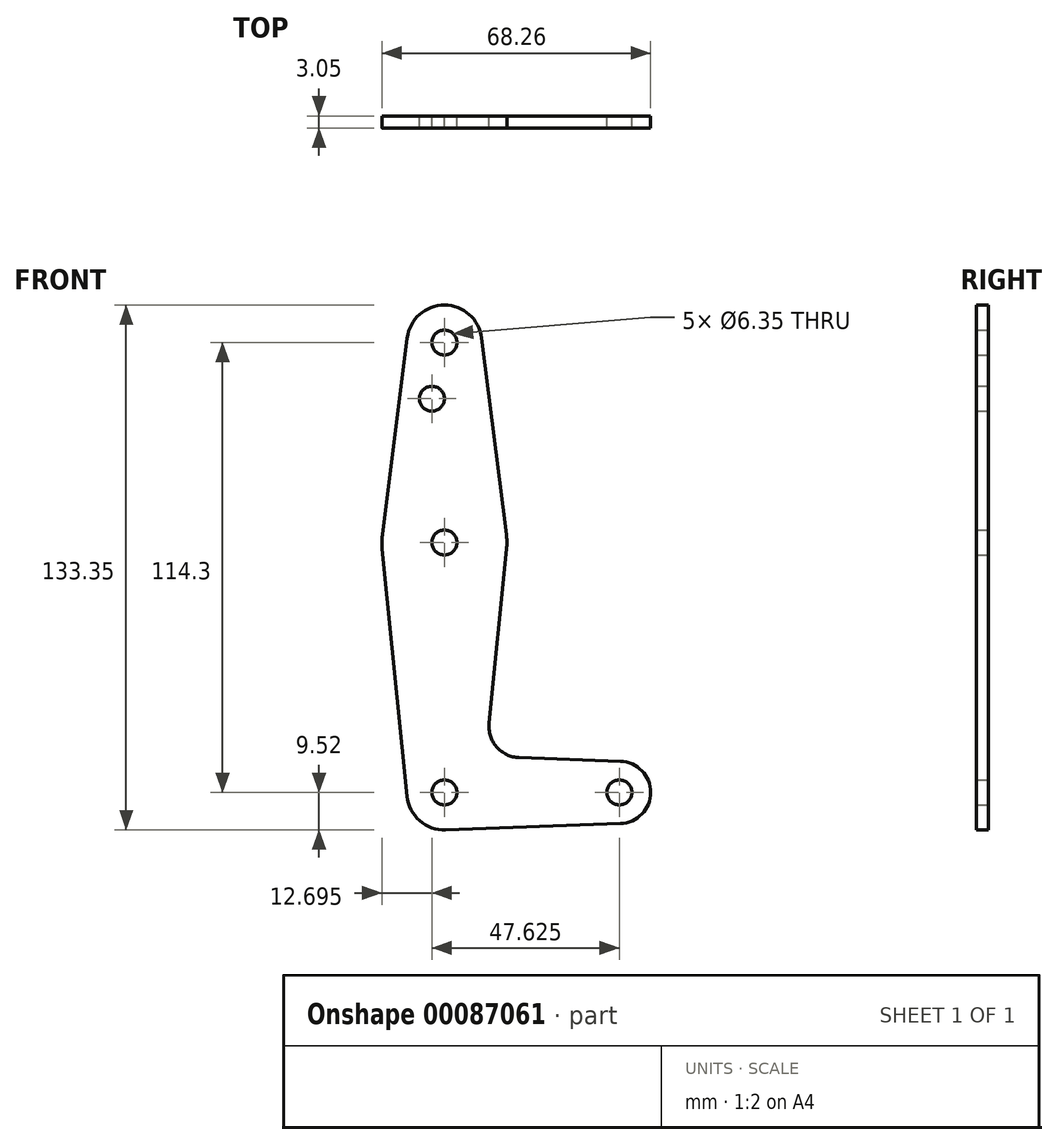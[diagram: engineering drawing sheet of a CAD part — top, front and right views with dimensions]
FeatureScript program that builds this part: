
annotation { "Feature Type Name" : "Feature", "Feature Type Description" : "" }
export const myFeature = defineFeature(function(context is Context, id is Id, definition is map)
    precondition{}
    {
        {
            var Q0;
            Q0=qCreatedBy(makeId("Front.planeOp"),FACE);
            var sketch = newSketch(context, id + "F0", { "sketchPlane" : qUnion([Q0])});
            skLineSegment(sketch, "E0", {"start": v(0, 114.3) * mm, "end": v(0, 0) * mm, "construction": true});
            skLineSegment(sketch, "E1", {"start": v(0, 0) * mm, "end": v(44.45, 0) * mm, "construction": true});
            skCircle(sketch, "E2", {"center": v(0, 114.3) * mm, "radius": 9.53 * mm});
            skCircle(sketch, "E3", {"center": v(0, 63.5) * mm, "radius": 15.88 * mm});
            skCircle(sketch, "E4", {"center": v(0, 0) * mm, "radius": 9.53 * mm});
            skCircle(sketch, "E5", {"center": v(44.45, 0) * mm, "radius": 7.94 * mm});
            skLineSegment(sketch, "E6", {"start": v(-9.45, 115.5) * mm, "end": v(-15.75, 65.48) * mm});
            skLineSegment(sketch, "E7", {"start": v(9.45, 115.5) * mm, "end": v(15.75, 65.48) * mm});
            skLineSegment(sketch, "E8", {"start": v(-15.8, 61.91) * mm, "end": v(-9.48, -0.95) * mm});
            skLineSegment(sketch, "E9", {"start": v(15.8, 61.91) * mm, "end": v(11.34, 17.6) * mm});
            skLineSegment(sketch, "E10", {"start": v(18.97, 8.85) * mm, "end": v(44.73, 7.93) * mm});
            skLineSegment(sketch, "E11", {"start": v(0.34, -9.52) * mm, "end": v(44.73, -7.93) * mm});
            skCircle(sketch, "E12", {"center": v(0, 114.3) * mm, "radius": 3.18 * mm});
            skCircle(sketch, "E13", {"center": v(-3.18, 100.03) * mm, "radius": 3.18 * mm});
            skCircle(sketch, "E14", {"center": v(0, 63.5) * mm, "radius": 3.18 * mm});
            skCircle(sketch, "E15", {"center": v(0, 0) * mm, "radius": 3.18 * mm});
            skCircle(sketch, "E16", {"center": v(44.45, 0) * mm, "radius": 3.18 * mm});
            skArc(sketch, "E17.filletArc", {"start": v(11.34, 17.6) * mm, "mid": v(13.26, 11.57) * mm, "end": v(18.97, 8.85) * mm});
            skSolve(sketch);
        }
        {
            var Q0;
            Q0=makeQuery(id+"F0.imprint","IMPRINT",FACE,{"disambiguationData":[TD([[makeQuery(id+"F0.imprint","IMPRINT",EDGE,{"derivedFrom":sQuery(id+"F0.wireOp",EDGE,"E12")}),-1.0]])]});
            var Q1;
            {var subQ1=sQuery(id+"F0.wireOp",EDGE,"E6");Q1=makeQuery(id+"F0.imprint","IMPRINT",FACE,{"disambiguationData":[TD([[makeQuery(id+"F0.imprint","IMPRINT",EDGE,{"derivedFrom":subQ1}),1.0]])]});}
            var Q2;
            {var subQ0=sQuery(id+"F0.wireOp",EDGE,"E8");Q2=makeQuery(id+"F0.imprint","IMPRINT",FACE,{"disambiguationData":[TD([[makeQuery(id+"F0.imprint","IMPRINT",EDGE,{"derivedFrom":subQ0}),1.0]])]});}
            var Q3;
            Q3=makeQuery(id+"F0.imprint","IMPRINT",FACE,{"disambiguationData":[TD([[makeQuery(id+"F0.imprint","IMPRINT",EDGE,{"derivedFrom":sQuery(id+"F0.wireOp",EDGE,"E14")}),-1.0]])]});
            var Q4;
            Q4=makeQuery(id+"F0.imprint","IMPRINT",FACE,{"disambiguationData":[TD([[makeQuery(id+"F0.imprint","IMPRINT",EDGE,{"derivedFrom":sQuery(id+"F0.wireOp",EDGE,"E15")}),-1.0]])]});
            var Q5;
            Q5=makeQuery(id+"F0.imprint","IMPRINT",FACE,{"disambiguationData":[TD([[makeQuery(id+"F0.imprint","IMPRINT",EDGE,{"derivedFrom":sQuery(id+"F0.wireOp",EDGE,"E16")}),-1.0]])]});
            extrude(context, id + "F1", {"entities" : qUnion([Q0, Q1, Q2, Q3, Q4, Q5]), "depth" : 3.05 * mm});
        }
    });
